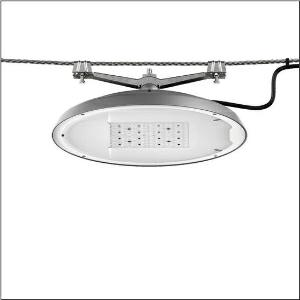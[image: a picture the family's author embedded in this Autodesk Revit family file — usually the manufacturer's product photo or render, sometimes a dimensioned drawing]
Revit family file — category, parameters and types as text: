
# Revit family: dl_r__50_iq_mini___st1_0s_5xa248w41f08me_9ef6
name_source: partatom
category: Lighting Fixtures
units: mm (PartAtom-declared; Revit-internal decimal feet)

## family parameters
Cut with Voids When Loaded = No
Host = Face
Light Source = No
Part Type = Normal
Room Calculation Point = No
Round Connector Dimension = Use Diameter
Shared = No

## types (1)
- --- (1 x LED, 15660 lm, 101.7 W, 4000K)
    Apparent Load = 102 VA
    CIE Flux Codes = 37 72 97 100 100
    Color Rendering = 70
    Color Temperature = 4000K
    Default Elevation = 1800 mm
    Description = DL® 50 iQ mini, catenary luminaire, primary light control with lens, of PMMA, primary optical cover: cover, of toughened safety glass, transparent, light distribution: ST1.0s, light emission: direct distribution, primary light characteristic: symmetric, installation type: suspended mounting, LED, High Power LED, rated luminous flux: 15.660lm, luminous efficacy: 154lm/W, light colour: 740, colour temperature: 4000K, control: optimised constant luminous flux control (CLO 2.0), Desk-Remote (wireless, voltage-free reading and setting of iQ features in the workshop via application-optimized NFC function/RFID function), Light-Fading, Smart-Wire, Night-Set, Lumen-Switch, Temp-Guard, Auto-Match, Street-Remote, mains connection: 230..240V, AC, 50/60Hz, start of lifetime: 102W, end of service life: 111W, reduction: 45W, luminaire housing, of diecast aluminium, powder-coated, Siteco® metallic grey (DB 702S), diameter: 500mm, height: 115mm, protection rating (complete): IP66, insulation class (complete): insulation class II (safety insulation), certification: CE, ENEC, VDE, impact resistance: IK08, permissible operating ambient temperature for outdoor applications: -25..+40°C, standard-compliant lighting for roads and squares, packaging unit: 1 piece

Light Distribution: ST1.0s
    Height = 124 mm  [stored 0.406824 ft]
    Lamp = 1 x LED
    Lamp Light Flux = 15660 lm
    Lamp Power = 101.7 W
    Lamp count = 1
    Length = 500 mm
    Luminous efficacy = 154 lm/W
    Manufacturer = Siteco
    ModVariant = No
    Model = 5XA248W41F08ME
    Number of Poles = 1
    OnlyDefault = Yes
    Power Factor = 1
    Product Name = DL® 50 iQ mini | ST1.0s
    Product group = catenary luminaire
    ProductGroupID = 6300
    Protection Class = Protection class II
    Protection Degree = IP 66
    RLX_Detail_Level = 1
    RLX_Emergency_Light_Flux = 0 lm
    RLX_Emergency_Type = 0
    RLX_Emergency_Type_DB = No
    RlxData = <blob elided: 127221 chars, md5=b1d865f2>
    Socket = socket
    Standby Power = 0 W
    System Light Flux = 15660 lm
    System Power = 102 W
    Type Comments = factory setting: luminous flux: 100 % | dim-lin: 254 | 534 mA
    Type Image = l_1251783.jpg
    URL = http://relux.com
    VarID = @adj_071699
    Voltage = 0 V
    Weight = 0.00 kg
    Width = 0 mm  [stored 0 ft]

note: [stored X ft] marks values corroborated as IEEE doubles in the binary element streams (Revit-internal decimal feet)

## geometry (parser evidence)
native form markers: Blend x4, Sweep x15
no freeform markers — native parametric forms only
